# Revit family: bfs-30_150sya2_60Hz
name_source: partatom
category: 機械設備
units: mm (PartAtom-declared; Revit-internal decimal feet)

## family parameters
OmniClass タイトル = Centrifugal Fans
OmniClass 番号 = 23.75.35.17.27
パーツ タイプ = 割り込み
ロード時にボイドで切り取り = いいえ
丸型コネクタ寸法 = 直径を使用
作業面ベース = いいえ
共有 = いいえ
常に垂直 = はい
部屋計算ポイント = はい

## types (6) — shared parameters
Clearance Left = 600
IfcExportAs = IfcFanType
IfcExportType = CENTRIFUGALFORWARDCURVED
MID静圧 = 0.0 Pa
MID風量 = 0.0 m³/h
MIN静圧 = 0.0 Pa
MIN風量 = 0.0 m³/h
OmniClassCode = 23-33 31 19 13 15
URL = https://www.mitsubishielectric.co.jp
Uniclass2015Code = Pr_65_67_29_12
Uniclass2015Title = Centrifugal fans
Uniclass2015Version = Systems v1.9
サービススペース = はい
ドレン管径 = 18 mm
ファンの種類 = 多翼形
仕様書バージョン = Version1.0
企業コード = 108420
分類コード = 50052502100020
周波数 = 60 Hz
呼称 = 消音ボックス付送風機
実風量 = 0.0 m³/h
形名 = BFS-SYA : BFS-30SYA
本体マテリアル = 溶融亜鉛めっき鋼板
極 = 4
極数 = 2
法定耐用年数 = 15
盤工事区分 = 電気工事
相 = 1
積算_科目 = 2 換気設備
製品リリース年月 = 2022年6月1日
製品出荷対象 = 国内
製造元 = 三菱電機株式会社
設置方法 = 天吊
説明 = ストレートシロッコファン消音形耐湿タイプ
負荷分類 = 3_ファン類
運転質量 = 0.00 kg
電圧 = 100 V
zero-valued in all types: Clearance Back, Clearance Bottom, Clearance Front, Clearance Right, Clearance Top

## per-type parameters (varying)
| type | Depth | Height | M | MAX静圧 | MAX風量 | Width | ダクト径 | 価格 | 参照している仕様書等のバージョン | 天吊金具ピッチ奥行 | 天吊金具ピッチ幅 | 消費電力 | 番手 | 製品質量 | 質量 | 電動機出力 | 騒音レベル(dB(A)) | 騒音レベル(dB(A))_側面 | 騒音レベル(dB(A))_吐出 | 騒音レベル(dB(A))_吸込 |
| BFS-30SYA2 | 335  [stored 1.09908 ft] | 228.4  [stored 0.749344 ft] | 70  [stored 0.229659 ft] | 39.0 Pa | 300.0 m³/h | 223  [stored 0.731627 ft] | 150 mm | 110000 $ |  | 300  [stored 0.984252 ft] | 299  [stored 0.980971 ft] | 44 W | #1 | 7.00 kg | 8.40 kg | 16 W | 40 | 24.5 | 40 | 37.5 |
| BFS-40SYA2 | 388  [stored 1.27297 ft] | 258.4  [stored 0.847769 ft] | 70  [stored 0.229659 ft] | 69.0 Pa | 400.0 m³/h | 255  [stored 0.836614 ft] | 150 mm | 119000 $ |  | 353  [stored 1.15814 ft] | 331  [stored 1.08596 ft] | 66 W | #1 1/4 | 9.50 kg | 11.40 kg | 25 W | 44 | 27 | 44 | 38 |
| BFS-50SYA2 | 423  [stored 1.3878 ft] | 258.4  [stored 0.847769 ft] | 85  [stored 0.278871 ft] | 175.0 Pa | 500.0 m³/h | 325  [stored 1.06627 ft] | 200 mm | 161000 $ | 公共建築工事標準仕様書（機械設備工事編）平成31年度版 | 388  [stored 1.27297 ft] | 401  [stored 1.31562 ft] | 88 W | #1 1/4 | 12.50 kg | 15.00 kg | 45 W | 49 | 26.5 | 49 | 39 |
| BFS-80SYA2 | 488  [stored 1.60105 ft] | 308.4  [stored 1.01181 ft] | 85  [stored 0.278871 ft] | 157.0 Pa | 800.0 m³/h | 373  [stored 1.22375 ft] | 200 mm | 179000 $ | 公共建築工事標準仕様書（機械設備工事編）平成31年度版 | 453  [stored 1.48622 ft] | 449  [stored 1.4731 ft] | 155 W | #1 1/4 | 15.00 kg | 18.00 kg | 80 W | 53 | 31 | 53 | 40.5 |
| BFS-100SYA2 | 488  [stored 1.60105 ft] | 308.4  [stored 1.01181 ft] | 85  [stored 0.278871 ft] | 250.0 Pa | 1000.0 m³/h | 393  [stored 1.28937 ft] | 200 mm | 204000 $ | 公共建築工事標準仕様書（機械設備工事編）平成31年度版 | 453  [stored 1.48622 ft] | 469 | 247 W | #1 1/2 | 18.00 kg | 21.60 kg | 160 W | 58 | 34 | 58 | 44.5 |
| BFS-150SYA2 | 590  [stored 1.9357 ft] | 353.4  [stored 1.15945 ft] | 85  [stored 0.278871 ft] | 265.0 Pa | 1500.0 m³/h | 391 | 250 mm | 234000 $ | 公共建築工事標準仕様書（機械設備工事編）平成31年度版 | 555  [stored 1.82087 ft] | 467  [stored 1.53215 ft] | 498 W | #1 1/2 | 21.50 kg | 25.80 kg | 340 W | 63 | 38 | 63 | 50.5 |

note: column(s) folded — value = type name in every type: モデル

note: [stored X ft] marks values corroborated as IEEE doubles in the binary element streams (Revit-internal decimal feet)
